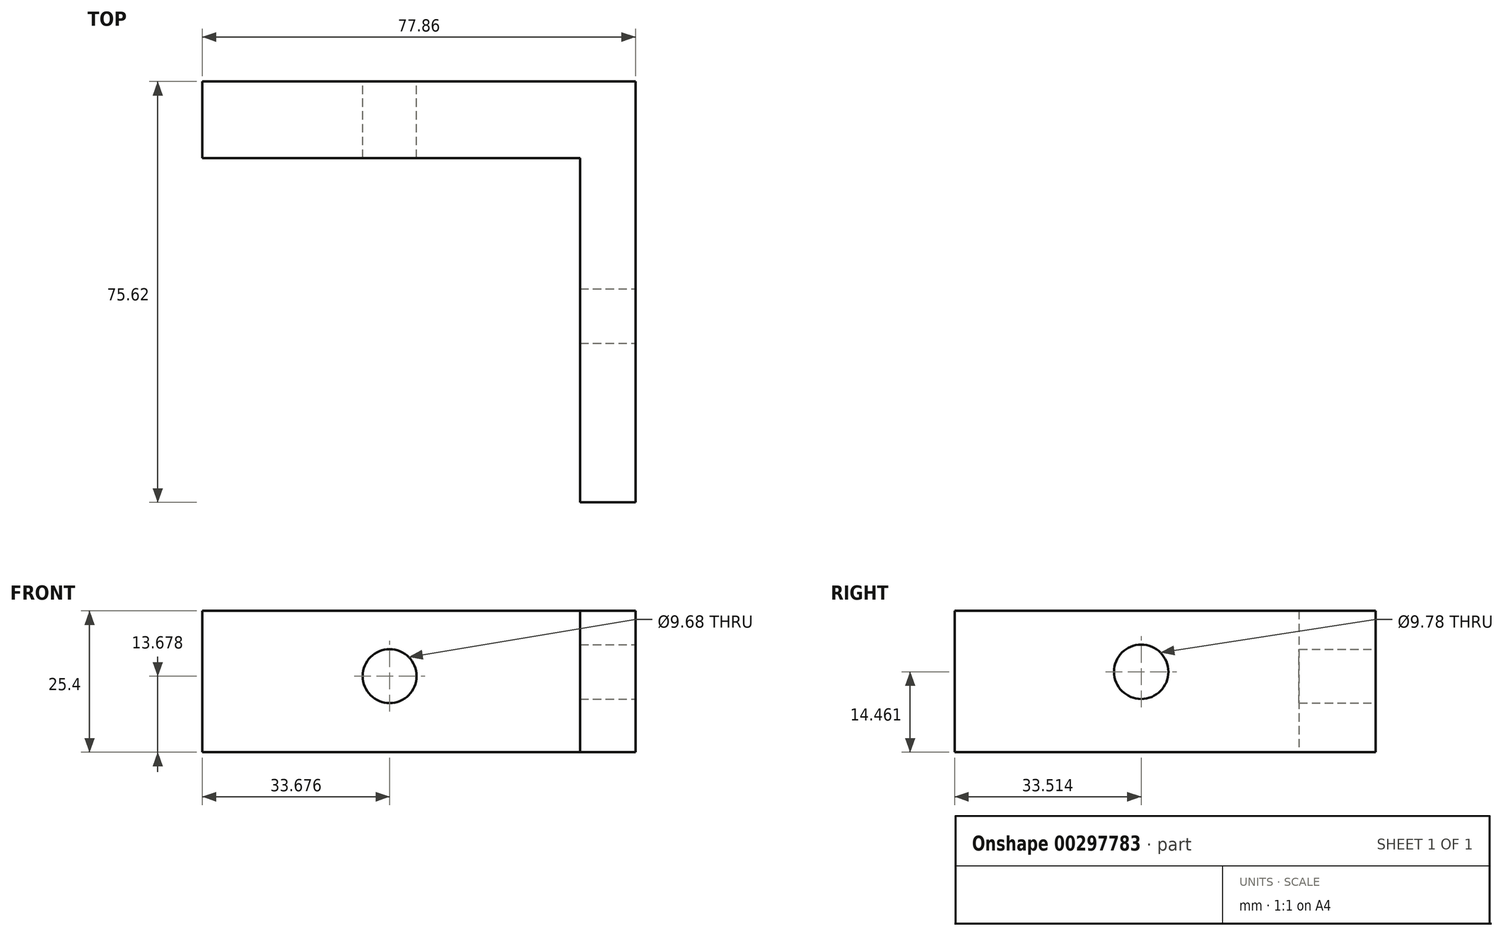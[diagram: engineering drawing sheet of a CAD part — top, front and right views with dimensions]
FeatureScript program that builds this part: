
annotation { "Feature Type Name" : "Feature", "Feature Type Description" : "" }
export const myFeature = defineFeature(function(context is Context, id is Id, definition is map)
    precondition{}
    {
        {
            var Q0;
            Q0=qCreatedBy(makeId("Top.planeOp"),FACE);
            var sketch = newSketch(context, id + "F0", { "sketchPlane" : qUnion([Q0])});
            skLineSegment(sketch, "E0", {"start": v(-48.5, 35.01) * mm, "end": v(29.37, 35.01) * mm});
            skLineSegment(sketch, "E1", {"start": v(29.37, 35.01) * mm, "end": v(29.37, -40.6) * mm});
            skLineSegment(sketch, "E2", {"start": v(29.37, -40.6) * mm, "end": v(19.42, -40.6) * mm});
            skLineSegment(sketch, "E3", {"start": v(19.42, -40.6) * mm, "end": v(19.42, 21.28) * mm});
            skLineSegment(sketch, "E4", {"start": v(19.42, 21.28) * mm, "end": v(-48.5, 21.28) * mm});
            skLineSegment(sketch, "E5", {"start": v(-48.5, 35.01) * mm, "end": v(-48.5, 18.5) * mm});
            skSolve(sketch);
        }
        {
            var Q0;
            {var subQ0=sQuery(id+"F0.wireOp",EDGE,"E0");Q0=makeQuery(id+"F0.imprint","IMPRINT",FACE,{"disambiguationData":[TD([[makeQuery(id+"F0.imprint","IMPRINT",EDGE,{"derivedFrom":subQ0}),-1.0]])]});}
            extrude(context, id + "F1", {"entities" : qUnion([Q0]), "depth" : 25.4 * mm});
        }
        {
            var Q0;
            Q0=makeQuery(id+"F1.opExtrude","SWEPT_FACE",FACE,{"disambiguationData":[OSD([sQuery(id+"F0.wireOp",EDGE,"E1")])]});
            var sketch = newSketch(context, id + "F2", { "sketchPlane" : qUnion([Q0])});
            skCircle(sketch, "E6", {"center": v(-7.1, 14.46) * mm, "radius": 4.89 * mm});
            skSolve(sketch);
        }
        {
            var Q0;
            Q0=makeQuery(id+"F2.imprint","IMPRINT",FACE,{"disambiguationData":[TD([[makeQuery(id+"F2.imprint","IMPRINT",EDGE,{"derivedFrom":sQuery(id+"F2.wireOp",EDGE,"E6")}),1.0]])]});
            var Q1;
            Q1=sQuery(id+"F2.wireOp",EDGE,"E6");
            extrude(context, id + "F3", {"entities" : qUnion([Q0]), "operationType" : NewBodyOperationType.REMOVE, "surfaceEntities" : qUnion([Q1]), "oppositeDirection" : true, "depth" : 25.4 * mm});
        }
        {
            var Q0;
            Q0=makeQuery(id+"F1.opExtrude","SWEPT_FACE",FACE,{"disambiguationData":[OSD([sQuery(id+"F0.wireOp",EDGE,"E0")])]});
            var sketch = newSketch(context, id + "F4", { "sketchPlane" : qUnion([Q0])});
            skCircle(sketch, "E7", {"center": v(14.81, 13.68) * mm, "radius": 4.84 * mm});
            skSolve(sketch);
        }
        {
            var Q0;
            Q0=makeQuery(id+"F4.imprint","IMPRINT",FACE,{"disambiguationData":[TD([[makeQuery(id+"F4.imprint","IMPRINT",EDGE,{"derivedFrom":sQuery(id+"F4.wireOp",EDGE,"E7")}),1.0]])]});
            var Q1;
            Q1=sQuery(id+"F4.wireOp",EDGE,"E7");
            extrude(context, id + "F5", {"entities" : qUnion([Q0]), "operationType" : NewBodyOperationType.REMOVE, "surfaceEntities" : qUnion([Q1]), "oppositeDirection" : true, "depth" : 14.48 * mm});
        }
    });
